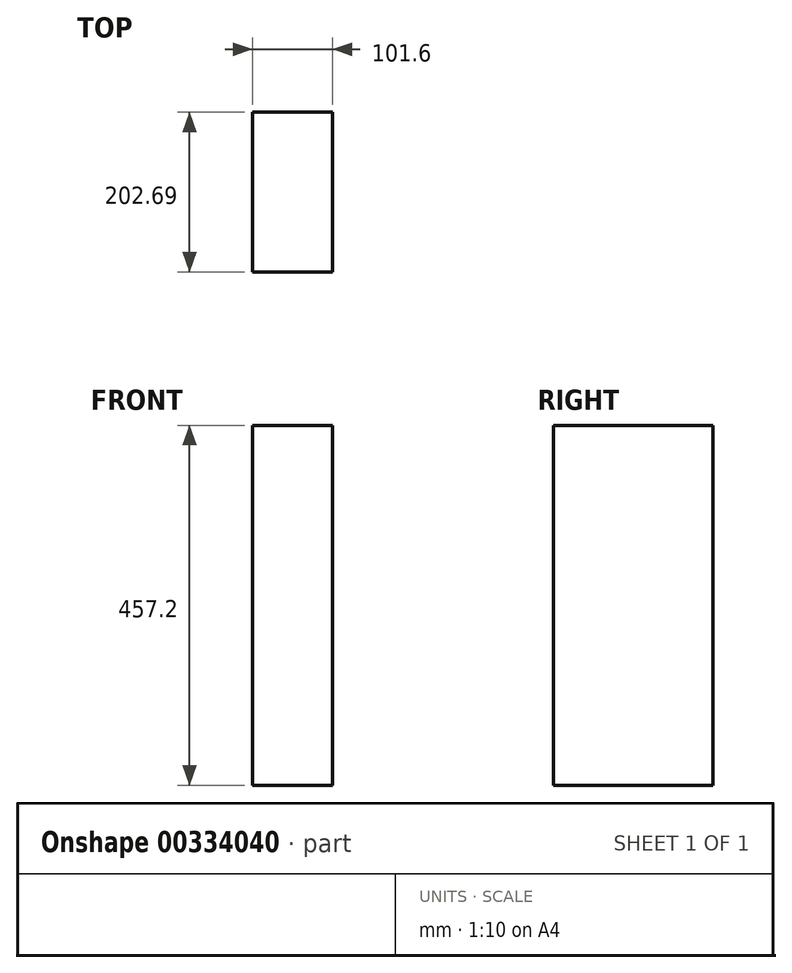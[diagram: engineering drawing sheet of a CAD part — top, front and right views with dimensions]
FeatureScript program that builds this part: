
annotation { "Feature Type Name" : "Feature", "Feature Type Description" : "" }
export const myFeature = defineFeature(function(context is Context, id is Id, definition is map)
    precondition{}
    {
        {
            var Q0;
            Q0=qCreatedBy(makeId("Front.planeOp"),FACE);
            var sketch = newSketch(context, id + "F0", { "sketchPlane" : qUnion([Q0])});
            skLineSegment(sketch, "E0.bottom", {"start": v(-33.03, 424.54) * mm, "end": v(68.57, 424.54) * mm});
            skLineSegment(sketch, "E0.top", {"start": v(-33.03, -32.66) * mm, "end": v(68.57, -32.66) * mm});
            skLineSegment(sketch, "E0.left", {"start": v(-33.03, 424.54) * mm, "end": v(-33.03, -32.66) * mm});
            skLineSegment(sketch, "E0.right", {"start": v(68.57, 424.54) * mm, "end": v(68.57, -32.66) * mm});
            skSolve(sketch);
        }
        {
            var Q0;
            Q0 = qSketchRegion(id + "F0", true);
            extrude(context, id + "F1", {"entities" : qUnion([Q0]), "depth" : 202.7 * mm});
        }
    });
